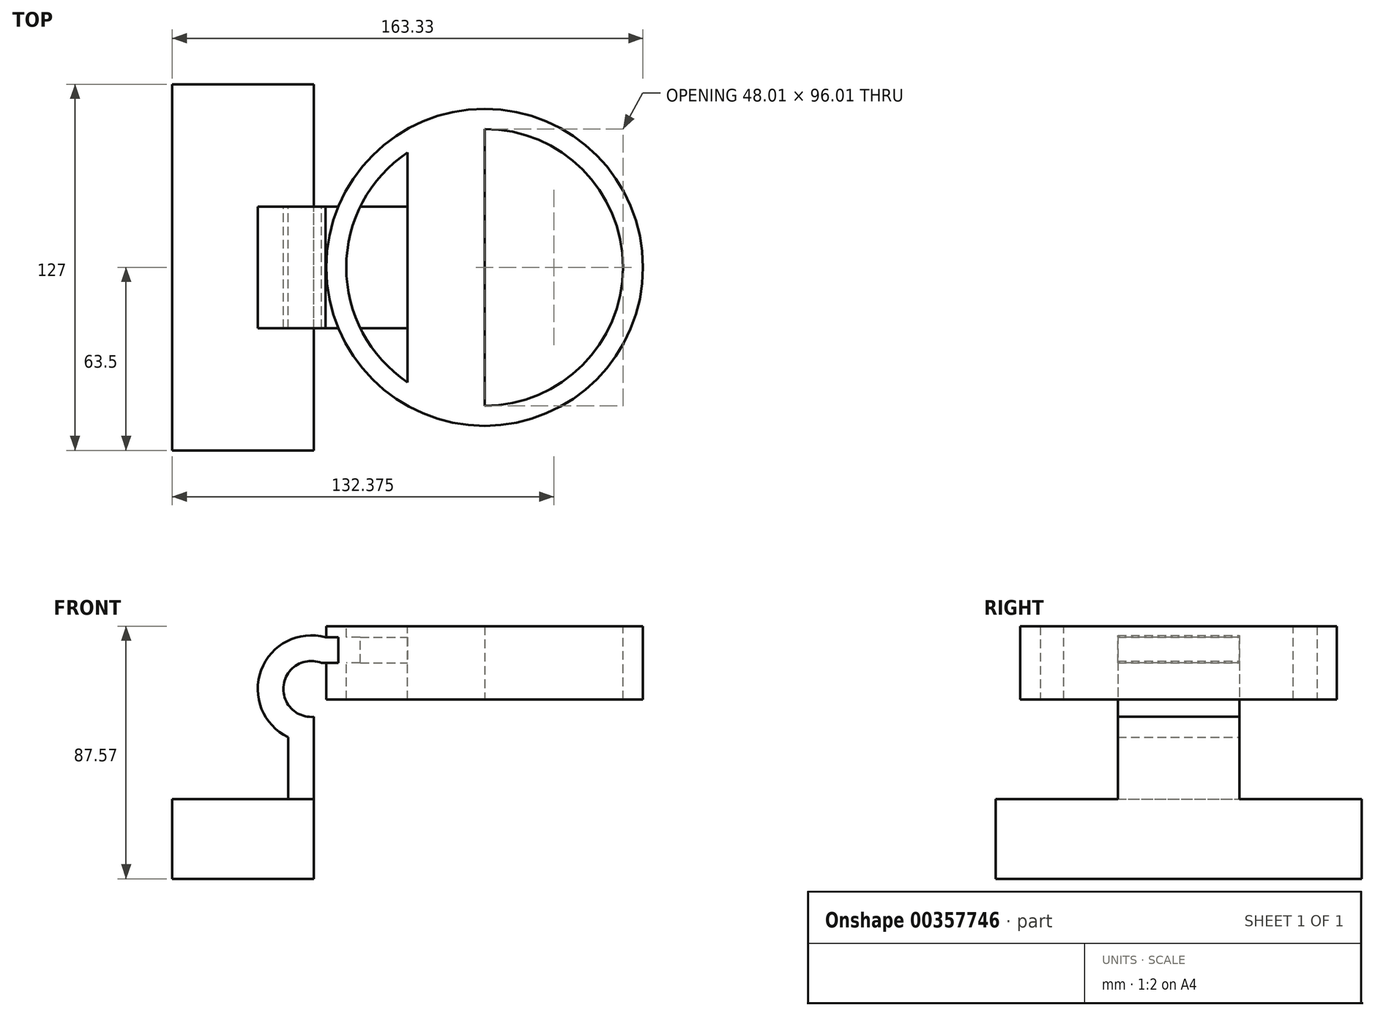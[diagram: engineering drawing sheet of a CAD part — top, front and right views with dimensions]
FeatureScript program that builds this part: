
annotation { "Feature Type Name" : "Feature", "Feature Type Description" : "" }
export const myFeature = defineFeature(function(context is Context, id is Id, definition is map)
    precondition{}
    {
        {
            var Q0;
            Q0=qCreatedBy(makeId("Front.planeOp"),FACE);
            var sketch = newSketch(context, id + "F0", { "sketchPlane" : qUnion([Q0])});
            skLineSegment(sketch, "E0.bottom", {"start": v(0, 0) * mm, "end": v(-49.05, 0) * mm});
            skLineSegment(sketch, "E0.top", {"start": v(0, -27.64) * mm, "end": v(-49.05, -27.64) * mm});
            skLineSegment(sketch, "E0.left", {"start": v(0, 0) * mm, "end": v(0, -27.64) * mm});
            skLineSegment(sketch, "E0.right", {"start": v(-49.05, 0) * mm, "end": v(-49.05, -27.64) * mm});
            skLineSegment(sketch, "E1.bottom", {"start": v(32.56, 59.93) * mm, "end": v(59.32, 59.93) * mm});
            skLineSegment(sketch, "E1.top", {"start": v(32.56, 34.53) * mm, "end": v(59.32, 34.53) * mm});
            skLineSegment(sketch, "E1.left", {"start": v(32.56, 59.93) * mm, "end": v(32.56, 34.53) * mm});
            skLineSegment(sketch, "E1.right", {"start": v(59.32, 59.93) * mm, "end": v(59.32, 34.53) * mm});
            skLineSegment(sketch, "E2", {"start": v(0, 0) * mm, "end": v(0, 28.53) * mm});
            skArc(sketch, "E3", {"start": v(2.75, 47.23) * mm, "mid": v(-10.4, 39.61) * mm, "end": v(0, 28.53) * mm});
            skLineSegment(sketch, "E4", {"start": v(2.75, 47.23) * mm, "end": v(32.56, 47.23) * mm});
            skLineSegment(sketch, "E5.0", {"start": v(4.16, 56.12) * mm, "end": v(32.67, 56.12) * mm});
            skArc(sketch, "E5.1", {"start": v(4.16, 56.12) * mm, "mid": v(-18.2, 44.75) * mm, "end": v(-8.9, 21.46) * mm});
            skLineSegment(sketch, "E5.2", {"start": v(-8.9, 0) * mm, "end": v(-8.9, 21.46) * mm});
            skSolve(sketch);
        }
        {
            var Q0;
            Q0=makeQuery(id+"F0.imprint","IMPRINT",FACE,{"disambiguationData":[TD([[makeQuery(id+"F0.imprint","IMPRINT",EDGE,{"derivedFrom":sQuery(id+"F0.wireOp",EDGE,"E0.top")}),-1.0]])]});
            extrude(context, id + "F1", {"entities" : qUnion([Q0]), "endBound" : BoundingType.SYMMETRIC, "depth" : 127 * mm});
        }
        {
            var Q0;
            {var subQ0=sQuery(id+"F0.wireOp",EDGE,"E2");Q0=makeQuery(id+"F0.imprint","IMPRINT",FACE,{"disambiguationData":[TD([[makeQuery(id+"F0.imprint","IMPRINT",EDGE,{"derivedFrom":subQ0}),1.0]])]});}
            extrude(context, id + "F2", {"entities" : qUnion([Q0]), "operationType" : NewBodyOperationType.ADD, "endBound" : BoundingType.SYMMETRIC, "depth" : 42.16 * mm});
        }
        {
            var Q0;
            {var subQ3=sQuery(id+"F0.wireOp",EDGE,"E1.bottom");Q0=makeQuery(id+"F0.imprint","IMPRINT",FACE,{"disambiguationData":[TD([[makeQuery(id+"F0.imprint","IMPRINT",EDGE,{"derivedFrom":subQ3}),-1.0]])]});}
            extrude(context, id + "F3", {"entities" : qUnion([Q0]), "operationType" : NewBodyOperationType.ADD, "endBound" : BoundingType.SYMMETRIC, "depth" : 96.01 * mm});
        }
        {
            var Q0;
            Q0=makeQuery(id+"F3.opExtrude","CAP_FACE",FACE,{"disambiguationData":[OSD([sQuery(id+"F0.wireOp",EDGE,"E1.bottom"),sQuery(id+"F0.wireOp",EDGE,"E1.top"),sQuery(id+"F0.wireOp",EDGE,"E1.left"),sQuery(id+"F0.wireOp",EDGE,"E1.right")])],"isStart":false});
            var Q1;
            Q1=sQuery(id+"F0.wireOp",EDGE,"E1.right");
            revolve(context, id + "F4", {"operationType" : NewBodyOperationType.ADD, "entities" : qUnion([Q0]), "axis" : qUnion([Q1]), "revolveType" : RevolveType.FULL});
        }
    });
